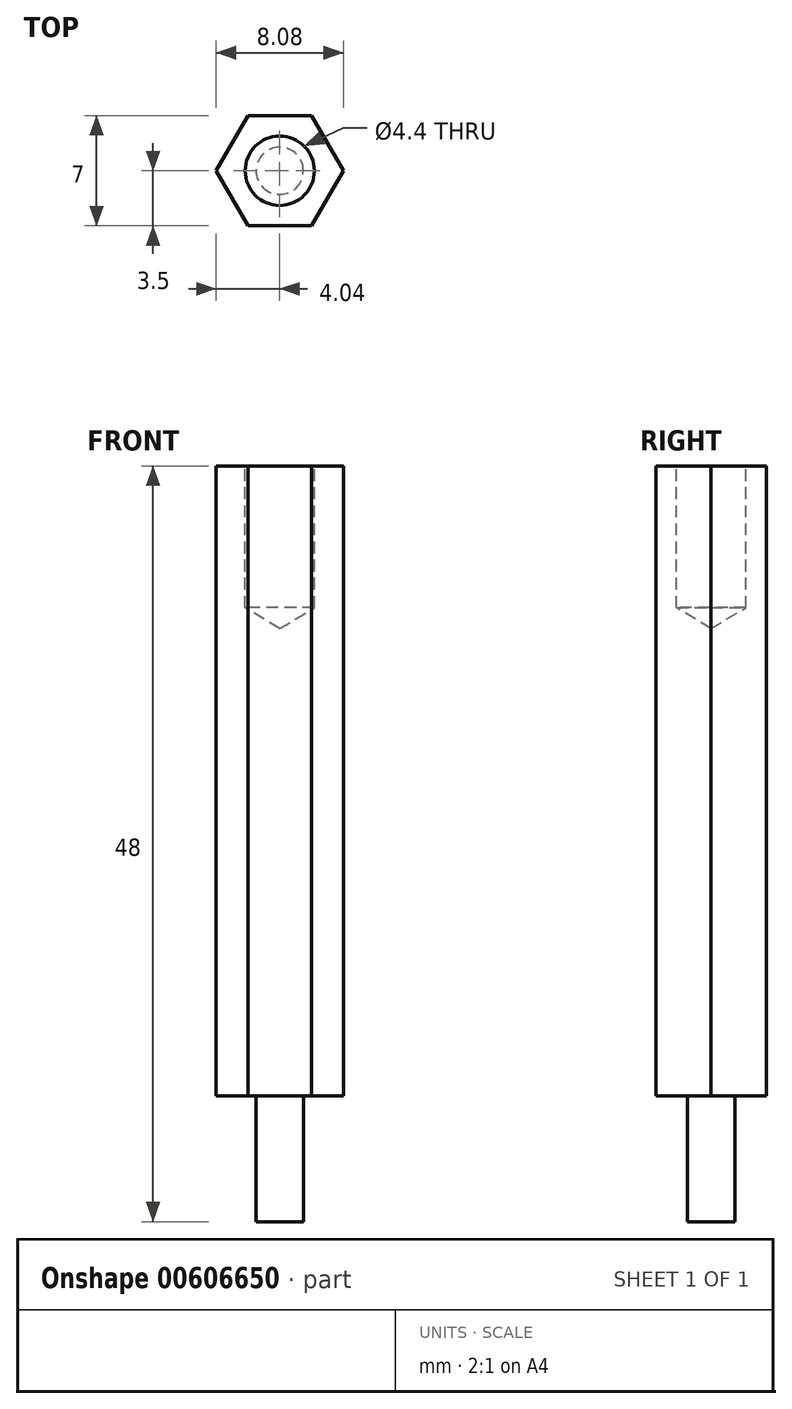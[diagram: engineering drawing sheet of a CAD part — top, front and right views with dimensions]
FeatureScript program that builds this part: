
annotation { "Feature Type Name" : "Feature", "Feature Type Description" : "" }
export const myFeature = defineFeature(function(context is Context, id is Id, definition is map)
    precondition{}
    {
        {
            var Q0;
            Q0=qCreatedBy(makeId("Top.planeOp"),FACE);
            var sketch = newSketch(context, id + "F0", { "sketchPlane" : qUnion([Q0])});
            skCircle(sketch, "E0.cCircle", {"center": v(0, 0) * mm, "radius": 3.5 * mm, "construction": true});
            skLineSegment(sketch, "E0.0", {"start": v(2.02, 3.5) * mm, "end": v(4.04, 0) * mm});
            skLineSegment(sketch, "E0.1", {"start": v(4.04, 0) * mm, "end": v(2.02, -3.5) * mm});
            skLineSegment(sketch, "E0.2", {"start": v(2.02, -3.5) * mm, "end": v(-2.02, -3.5) * mm});
            skLineSegment(sketch, "E0.3", {"start": v(-2.02, -3.5) * mm, "end": v(-4.04, 0) * mm});
            skLineSegment(sketch, "E0.4", {"start": v(-4.04, 0) * mm, "end": v(-2.02, 3.5) * mm});
            skLineSegment(sketch, "E0.5", {"start": v(-2.02, 3.5) * mm, "end": v(2.02, 3.5) * mm});
            skPoint(sketch, "E0.0.midPoint", {"position": v(3.03, 1.75) * mm});
            skCircle(sketch, "E1", {"center": v(0, 0) * mm, "radius": 1.5 * mm});
            skSolve(sketch);
        }
        {
            var Q0;
            Q0=makeQuery(id+"F0.imprint","IMPRINT",FACE,{"disambiguationData":[TD([[makeQuery(id+"F0.imprint","IMPRINT",EDGE,{"derivedFrom":sQuery(id+"F0.wireOp",EDGE,"E0.0")}),-1.0]])]});
            var Q1;
            Q1=makeQuery(id+"F0.imprint","IMPRINT",FACE,{"disambiguationData":[TD([[makeQuery(id+"F0.imprint","IMPRINT",EDGE,{"derivedFrom":sQuery(id+"F0.wireOp",EDGE,"E1")}),1.0]])]});
            extrude(context, id + "F1", {"entities" : qUnion([Q0, Q1]), "depth" : 40 * mm, "offsetDistance" : 25 * mm});
        }
        {
            var Q0;
            Q0=makeQuery(id+"F0.imprint","IMPRINT",FACE,{"disambiguationData":[TD([[makeQuery(id+"F0.imprint","IMPRINT",EDGE,{"derivedFrom":sQuery(id+"F0.wireOp",EDGE,"E1")}),1.0]])]});
            extrude(context, id + "F2", {"entities" : qUnion([Q0]), "operationType" : NewBodyOperationType.ADD, "oppositeDirection" : true, "depth" : 8 * mm, "offsetDistance" : 25 * mm});
        }
        {
            var Q0;
            Q0=makeQuery(id+"F1.opExtrude","CAP_FACE",FACE,{"disambiguationData":[OSD([sQuery(id+"F0.wireOp",EDGE,"E0.0"),sQuery(id+"F0.wireOp",EDGE,"E0.1"),sQuery(id+"F0.wireOp",EDGE,"E0.2"),sQuery(id+"F0.wireOp",EDGE,"E0.3"),sQuery(id+"F0.wireOp",EDGE,"E0.4"),sQuery(id+"F0.wireOp",EDGE,"E0.5")])],"isStart":false});
            var sketch = newSketch(context, id + "F3", { "sketchPlane" : qUnion([Q0])});
            skPoint(sketch, "E2.0", {"position": v(0, 0) * mm});
            skSolve(sketch);
        }
        {
            var Q0;
            Q0=sQuery(id+"F3.wireOp",VERTEX,"E2.0");
            var Q1;
            Q1=makeQuery(id+"F1.opExtrude","SWEPT_BODY",BODY,{"disambiguationData":[OSD([sQuery(id+"F0.wireOp",EDGE,"E0.0"),sQuery(id+"F0.wireOp",EDGE,"E0.1"),sQuery(id+"F0.wireOp",EDGE,"E0.2"),sQuery(id+"F0.wireOp",EDGE,"E0.3"),sQuery(id+"F0.wireOp",EDGE,"E0.4"),sQuery(id+"F0.wireOp",EDGE,"E0.5")])]});
            hole(context, id + "F4", {"style" : HoleStyle.SIMPLE, "endStyle" : HoleEndStyle.BLIND, "standardTappedOrClearance" : lookupTablePath({ "standard" : "ISO", "fit" : "Normal", "size" : "M4", "type" : "Clearance" }), "standardBlindInLast" : lookupTablePath({ "fit" : "Standard", "standard" : "ISO", "size" : "M4", "type" : "Clearance" }), "holeDiameter" : 4.4 * mm, "majorDiameter" : 5 * mm, "holeDepth" : 9 * mm, "isTappedThrough" : true, "tappedDepth" : 3.5 * mm, "tapClearance" : 3, "locations" : qUnion([Q0]), "scope" : qUnion([Q1])});
        }
    });
